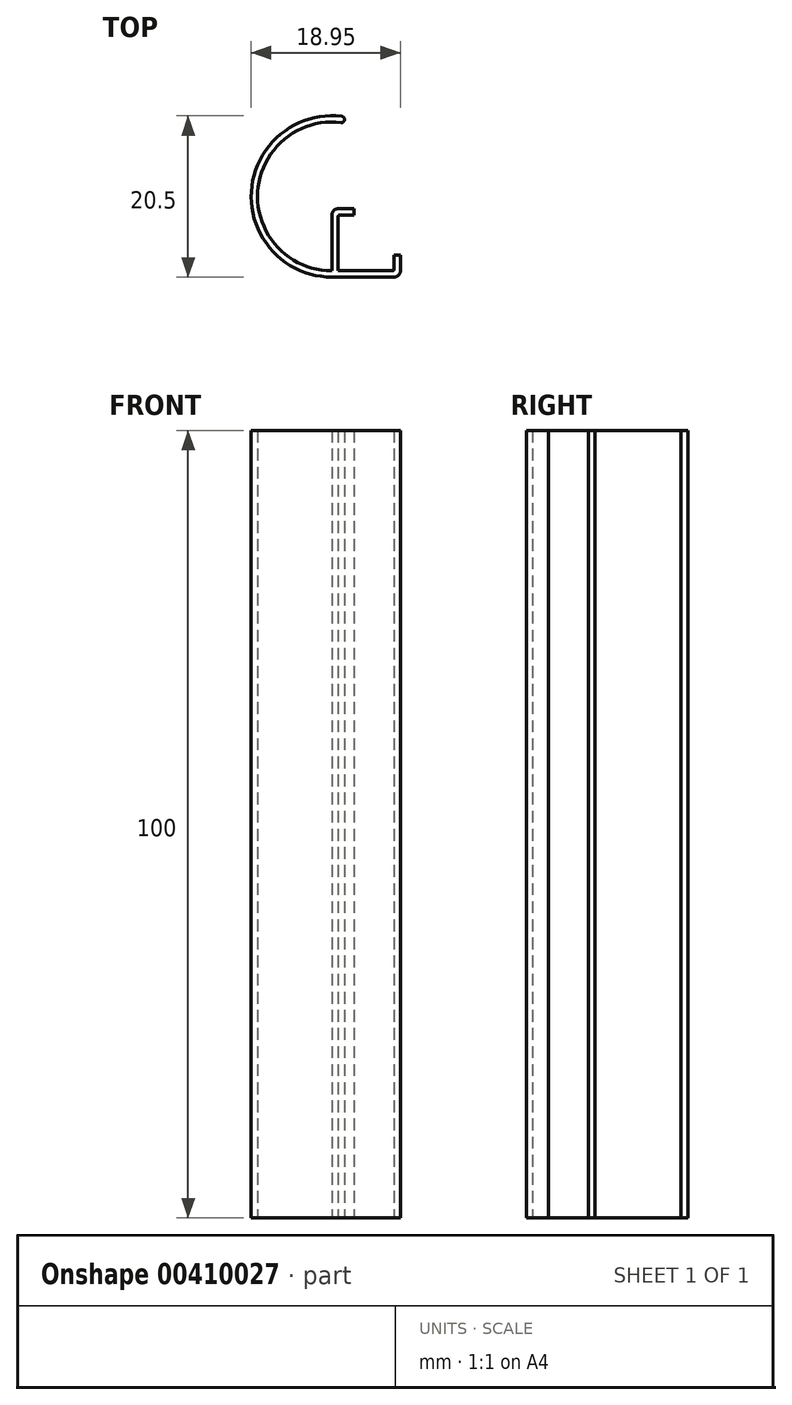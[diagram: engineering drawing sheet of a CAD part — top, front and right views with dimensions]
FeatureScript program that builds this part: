
annotation { "Feature Type Name" : "Feature", "Feature Type Description" : "" }
export const myFeature = defineFeature(function(context is Context, id is Id, definition is map)
    precondition{}
    {
        {
            var Q0;
            Q0=qCreatedBy(makeId("Top.planeOp"),FACE);
            var sketch = newSketch(context, id + "F0", { "sketchPlane" : qUnion([Q0])});
            skLineSegment(sketch, "E0", {"start": v(2.9, -8) * mm, "end": v(-2.9, -8) * mm});
            skLineSegment(sketch, "E1", {"start": v(-2.9, -8) * mm, "end": v(-2.9, -9.8) * mm});
            skLineSegment(sketch, "E2", {"start": v(-3.1, -10) * mm, "end": v(-10, -10) * mm});
            skLineSegment(sketch, "E3", {"start": v(-10, -10) * mm, "end": v(-10, -3.1) * mm});
            skLineSegment(sketch, "E4", {"start": v(-9.8, -2.9) * mm, "end": v(-8, -2.9) * mm});
            skLineSegment(sketch, "E5", {"start": v(-8, -2.9) * mm, "end": v(-8, 2.9) * mm});
            skLineSegment(sketch, "E6", {"start": v(-8, 2.9) * mm, "end": v(-10, 2.9) * mm});
            skLineSegment(sketch, "E7", {"start": v(-10, 2.9) * mm, "end": v(-10, 10) * mm});
            skLineSegment(sketch, "E8", {"start": v(-10, 10) * mm, "end": v(-2.9, 10) * mm});
            skLineSegment(sketch, "E9", {"start": v(-2.9, 10) * mm, "end": v(-2.9, 8) * mm});
            skLineSegment(sketch, "E10", {"start": v(-2.9, 8) * mm, "end": v(2.9, 8) * mm});
            skLineSegment(sketch, "E11", {"start": v(-10, -10) * mm, "end": v(0, 0) * mm, "construction": true});
            skLineSegment(sketch, "E12", {"start": v(0, 0) * mm, "end": v(-10, 10) * mm, "construction": true});
            skLineSegment(sketch, "E13.MirrorCS", {"start": v(2.9, 10) * mm, "end": v(2.9, 8) * mm});
            skLineSegment(sketch, "E14.MirrorCS", {"start": v(10, 2.9) * mm, "end": v(10, 10) * mm});
            skLineSegment(sketch, "E15.MirrorCS", {"start": v(8, 2.9) * mm, "end": v(10, 2.9) * mm});
            skLineSegment(sketch, "E16.MirrorCS", {"start": v(10, 10) * mm, "end": v(2.9, 10) * mm});
            skLineSegment(sketch, "E17.MirrorCS", {"start": v(8, -2.9) * mm, "end": v(8, 2.9) * mm});
            skLineSegment(sketch, "E18.MirrorCS", {"start": v(10, -2.9) * mm, "end": v(8, -2.9) * mm});
            skLineSegment(sketch, "E19.MirrorCS", {"start": v(10, -10) * mm, "end": v(10, -2.9) * mm});
            skLineSegment(sketch, "E20.MirrorCS", {"start": v(2.9, -10) * mm, "end": v(10, -10) * mm});
            skLineSegment(sketch, "E21.MirrorCS", {"start": v(2.9, -8) * mm, "end": v(2.9, -10) * mm});
            skCircle(sketch, "E22", {"center": v(-10.8, -0.55) * mm, "radius": 10.25 * mm});
            skLineSegment(sketch, "E23", {"start": v(-2.1, -8) * mm, "end": v(-2.1, -10) * mm});
            skLineSegment(sketch, "E24", {"start": v(-2.9, -10.8) * mm, "end": v(-10.8, -10.8) * mm});
            skLineSegment(sketch, "E25", {"start": v(-10.8, -10.8) * mm, "end": v(-10.8, -2.9) * mm});
            skLineSegment(sketch, "E26", {"start": v(-10, -2.1) * mm, "end": v(-8, -2.1) * mm});
            skCircle(sketch, "E27", {"center": v(-10.8, -0.55) * mm, "radius": 9.45 * mm});
            skCircle(sketch, "E28", {"center": v(-9.6, 9.23) * mm, "radius": 0.4 * mm});
            skPoint(sketch, "E29.visualSharp", {"position": v(-10.8, -2.1) * mm});
            skArc(sketch, "E29.filletArc", {"start": v(-10, -2.1) * mm, "mid": v(-10.57, -2.33) * mm, "end": v(-10.8, -2.9) * mm});
            skPoint(sketch, "E30.visualSharp", {"position": v(-2.1, -10.8) * mm});
            skArc(sketch, "E30.filletArc", {"start": v(-2.9, -10.8) * mm, "mid": v(-2.33, -10.57) * mm, "end": v(-2.1, -10) * mm});
            skArc(sketch, "E31.filletArc", {"start": v(-9.8, -2.9) * mm, "mid": v(-9.94, -2.96) * mm, "end": v(-10, -3.1) * mm});
            skArc(sketch, "E32.filletArc", {"start": v(-3.1, -10) * mm, "mid": v(-2.96, -9.94) * mm, "end": v(-2.9, -9.8) * mm});
            skSolve(sketch);
        }
        {
            var Q0;
            {var subQ0=sQuery(id+"F0.wireOp",EDGE,"E25");var subQ5=sQuery(id+"F0.wireOp",EDGE,"E27");var subQ6=makeQuery(id+"F0.imprint","INTERSECT",VERTEX,{"derivedFrom":[subQ0,subQ5]});Q0=makeQuery(id+"F0.imprint","IMPRINT",FACE,{"disambiguationData":[TD([[makeQuery(id+"F0.imprint","IMPRINT",EDGE,{"disambiguationData":[TD([[subQ6,1.0]])],"derivedFrom":subQ5}),-1.0]])]});}
            var Q1;
            {var subQ5=sQuery(id+"F0.wireOp",EDGE,"E4");Q1=makeQuery(id+"F0.imprint","IMPRINT",FACE,{"disambiguationData":[TD([[makeQuery(id+"F0.imprint","IMPRINT",EDGE,{"derivedFrom":subQ5}),1.0]])]});}
            var Q2;
            {var subQ5=sQuery(id+"F0.wireOp",EDGE,"E3");var subQ6=sQuery(id+"F0.wireOp",EDGE,"E2");var subQ7=makeQuery(id+"F0.imprint","INTERSECT",VERTEX,{"derivedFrom":[subQ6,subQ5]});Q2=makeQuery(id+"F0.imprint","IMPRINT",FACE,{"disambiguationData":[TD([[makeQuery(id+"F0.imprint","IMPRINT",EDGE,{"disambiguationData":[TD([[subQ7,1.0]])],"derivedFrom":subQ6}),1.0]])]});}
            var Q3;
            {var subQ4=sQuery(id+"F0.wireOp",EDGE,"E1");Q3=makeQuery(id+"F0.imprint","IMPRINT",FACE,{"disambiguationData":[TD([[makeQuery(id+"F0.imprint","IMPRINT",EDGE,{"derivedFrom":subQ4}),1.0]])]});}
            var Q4;
            {var subQ0=sQuery(id+"F0.wireOp",EDGE,"E28");var subQ1=makeQuery(id+"F0.imprint","INTERSECT",VERTEX,{"derivedFrom":[sQuery(id+"F0.wireOp",EDGE,"E22"),subQ0]});Q4=makeQuery(id+"F0.imprint","IMPRINT",FACE,{"disambiguationData":[TD([[makeQuery(id+"F0.imprint","IMPRINT",EDGE,{"disambiguationData":[TD([[subQ1,1.0]])],"derivedFrom":subQ0}),1.0]])]});}
            var Q5;
            {var subQ0=sQuery(id+"F0.wireOp",EDGE,"E22");var subQ1=sQuery(id+"F0.wireOp",EDGE,"E7");var subQ2=makeQuery(id+"F0.imprint","INTERSECT",VERTEX,{"derivedFrom":[subQ1,subQ0]});Q5=makeQuery(id+"F0.imprint","IMPRINT",FACE,{"disambiguationData":[TD([[makeQuery(id+"F0.imprint","IMPRINT",EDGE,{"disambiguationData":[TD([[subQ2,1.0]])],"derivedFrom":subQ1}),-1.0]])]});}
            var Q6;
            {var subQ0=sQuery(id+"F0.wireOp",EDGE,"E27");var subQ1=sQuery(id+"F0.wireOp",EDGE,"E7");var subQ2=makeQuery(id+"F0.imprint","INTERSECT",VERTEX,{"derivedFrom":[subQ1,subQ0]});Q6=makeQuery(id+"F0.imprint","IMPRINT",FACE,{"disambiguationData":[TD([[makeQuery(id+"F0.imprint","IMPRINT",EDGE,{"disambiguationData":[TD([[subQ2,-1.0]])],"derivedFrom":subQ1}),-1.0]])]});}
            extrude(context, id + "F1", {"entities" : qUnion([Q0, Q1, Q2, Q3, Q4, Q5, Q6]), "depth" : 100 * mm});
        }
    });
